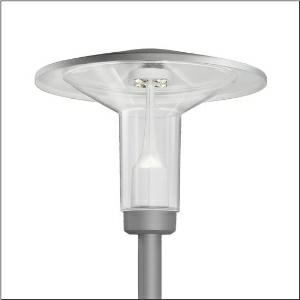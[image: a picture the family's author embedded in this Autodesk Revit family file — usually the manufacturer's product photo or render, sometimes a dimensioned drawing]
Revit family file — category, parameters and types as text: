
# Revit family: laterne_iq___p1_0a_5xa5255bf14h_d88c
name_source: partatom
category: Lighting Fixtures
units: mm (PartAtom-declared; Revit-internal decimal feet)

## family parameters
Cut with Voids When Loaded = No
Host = Face
Light Source = No
Part Type = Normal
Room Calculation Point = No
Round Connector Dimension = Use Diameter
Shared = No

## types (1)
- --- (1 x LED, 1510 lm, 12.9 W, 2200K)
    Apparent Load = 13 VA
    CIE Flux Codes = 35 64 91 96 100
    Color Rendering = 70
    Color Temperature = 2200K
    Default Elevation = 1800 mm
    Description = Lantern iQ, mast luminaire, Module 540 iQ-SR, primary light control with 3 zone facetted reflector, of plastic, silver coated, highly specular, structured, primary optical cover: cover, of PMMA, transparent, light distribution: P1.0a, light emission: direct distribution, primary light characteristic: strongly asymmetric, installation type: post-top, LED, High Power LED, rated luminous flux: 1.510lm, luminous efficacy: 117lm/W, light colour: 722, colour temperature: 2200K, control gear: ECG iQ, control: presetting dimming logarithmic, Street-Remote, Auto-Match, Temp-Guard, Lumen-Switch, Night-Set, Smart-Wire, Light-Fading, Desk-Remote (wireless, voltage-free reading and setting of iQ features in the workshop via application-optimized NFC function/RFID function), optimised constant luminous flux control (CLO 2.0), with terminal, 6-pole, max. 2.5mm², mains connection: 220..240V, AC, 50/60Hz, start of lifetime: 13W, end of lifetime: 13W, reduction: 6W, luminaire housing, upper part, of glass-fibre reinforced polyester, coated, Siteco® metallic grey (DB 702S), diameter: 750mm, height: 583mm, spigot size: d x l = 76 x 70mm (post-top) | with reducer (optional accessory) 60 x 70mm, post-top mast mounting element, of diecast aluminium, coated, Siteco® metallic grey (DB 702S), Module 540 iQ-SR, traffic white (RAL 9016), equipment: standard, protection rating (complete): IP65, insulation class (complete): insulation class II (safety insulation), certification: CE, ENEC, VDE, packaging unit: 1 piece

Light Distribution: P1.0a
    Height = 583 mm
    Lamp = 1 x LED
    Lamp Light Flux = 1510 lm
    Lamp Power = 12.9 W
    Lamp count = 1
    Length = 750 mm
    Luminous efficacy = 117 lm/W
    Manufacturer = Siteco
    ModVariant = No
    Model = 5XA5255BF14H
    Number of Poles = 1
    OnlyDefault = Yes
    Power Factor = 1
    Product Name = Laterne iQ | P1.0a
    Product group = mast luminaire | pylon top
    ProductGroupID = 6100
    Protection Class = Protection class II
    Protection Degree = IP 65
    RLX_Detail_Level = 1
    RlxData = <blob elided: 74305 chars, md5=670d94c1>
    Socket = socket
    Standby Power = 0 W
    System Light Flux = 1510 lm
    System Power = 13 W
    Type Comments = factory setting: luminous flux: 100 % | dim-lin: 254 | 516 mA
    Type Image = l_1006050.jpg
    URL = http://relux.com
    VarID = @adj_071783
    Voltage = 0 V
    Weight = 0.00 kg
    Width = 0 mm  [stored 0 ft]

note: [stored X ft] marks values corroborated as IEEE doubles in the binary element streams (Revit-internal decimal feet)

## geometry (parser evidence)
native form markers: Blend x4, Sweep x7
no freeform markers — native parametric forms only
